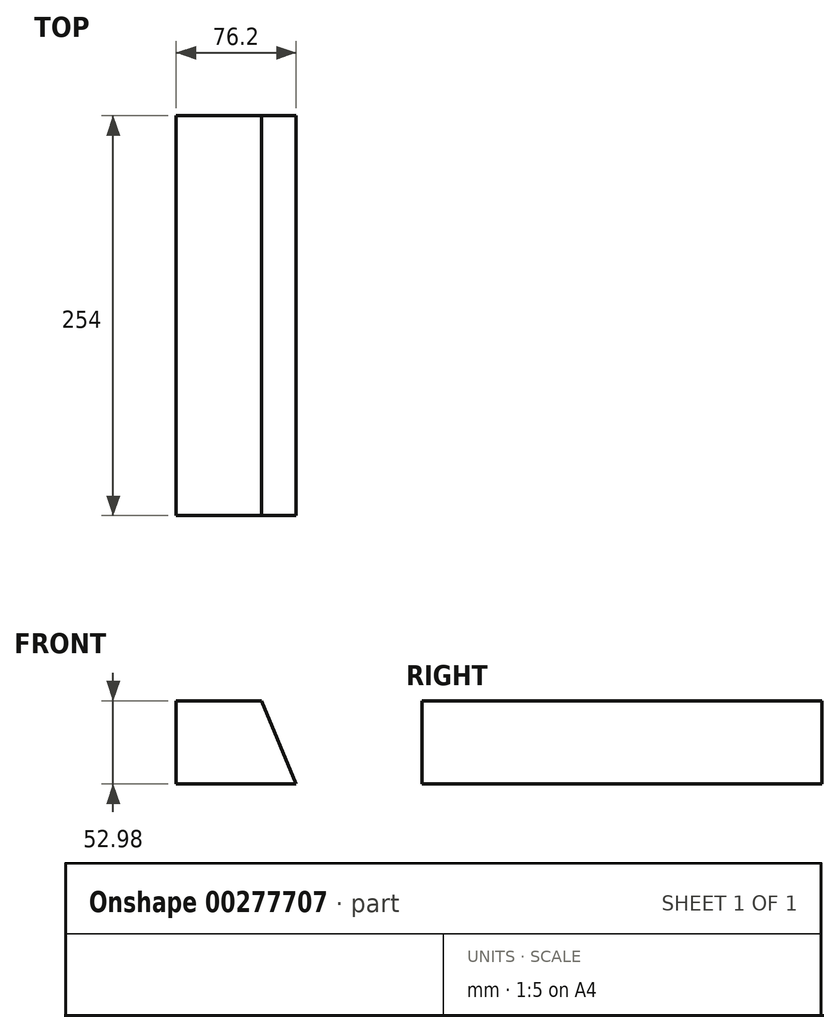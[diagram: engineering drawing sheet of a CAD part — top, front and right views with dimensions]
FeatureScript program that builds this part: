
annotation { "Feature Type Name" : "Feature", "Feature Type Description" : "" }
export const myFeature = defineFeature(function(context is Context, id is Id, definition is map)
    precondition{}
    {
        {
            var Q0;
            Q0=qCreatedBy(makeId("Front.planeOp"),FACE);
            var sketch = newSketch(context, id + "F0", { "sketchPlane" : qUnion([Q0])});
            skLineSegment(sketch, "E0", {"start": v(-63.98, 63.2) * mm, "end": v(-63.98, 10.22) * mm});
            skLineSegment(sketch, "E1", {"start": v(-63.98, 10.22) * mm, "end": v(12.22, 10.22) * mm});
            skLineSegment(sketch, "E2", {"start": v(12.22, 10.22) * mm, "end": v(-9.72, 63.2) * mm});
            skLineSegment(sketch, "E3", {"start": v(-9.72, 63.2) * mm, "end": v(-63.98, 63.2) * mm});
            skSolve(sketch);
        }
        {
            var Q0;
            Q0 = qSketchRegion(id + "F0", true);
            extrude(context, id + "F1", {"entities" : qUnion([Q0]), "depth" : 254 * mm});
        }
    });
